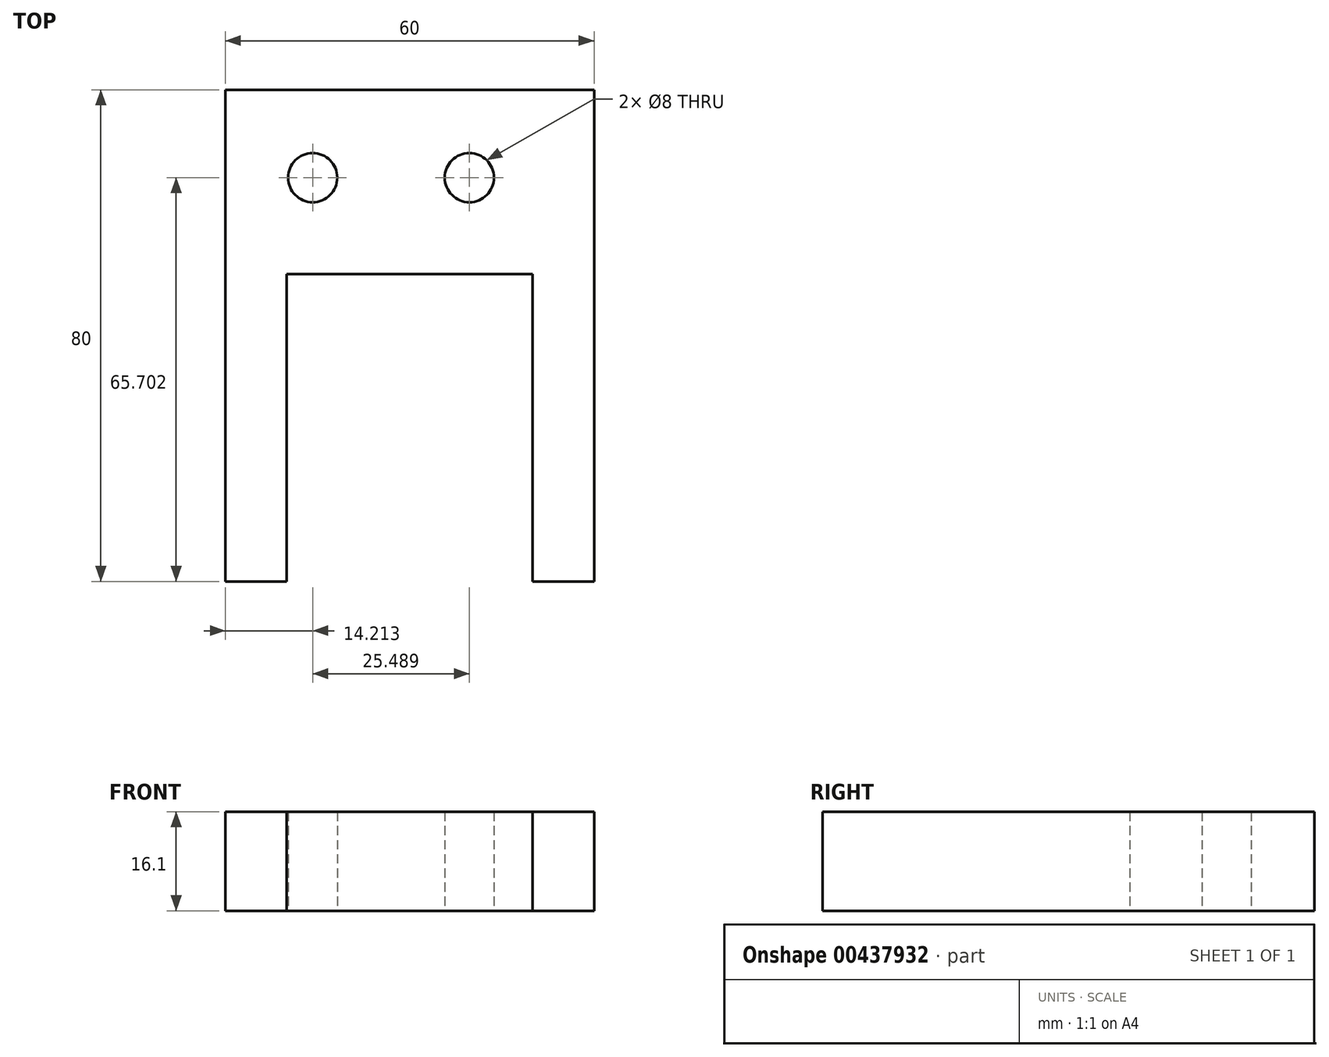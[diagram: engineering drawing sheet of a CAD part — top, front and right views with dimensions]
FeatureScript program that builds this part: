
annotation { "Feature Type Name" : "Feature", "Feature Type Description" : "" }
export const myFeature = defineFeature(function(context is Context, id is Id, definition is map)
    precondition{}
    {
        {
            var Q0;
            Q0=qCreatedBy(makeId("Top.planeOp"),FACE);
            var sketch = newSketch(context, id + "F0", { "sketchPlane" : qUnion([Q0])});
            skLineSegment(sketch, "E0.bottom", {"start": v(-53.14, 69.79) * mm, "end": v(6.86, 69.79) * mm});
            skLineSegment(sketch, "E0.top", {"start": v(-53.14, 39.79) * mm, "end": v(6.86, 39.79) * mm});
            skLineSegment(sketch, "E0.left", {"start": v(-53.14, 69.79) * mm, "end": v(-53.14, 39.79) * mm});
            skLineSegment(sketch, "E0.right", {"start": v(6.86, 69.79) * mm, "end": v(6.86, 39.79) * mm});
            skLineSegment(sketch, "E1.bottom", {"start": v(-53.14, 39.79) * mm, "end": v(-43.14, 39.79) * mm});
            skLineSegment(sketch, "E1.top", {"start": v(-53.14, -10.21) * mm, "end": v(-43.14, -10.21) * mm});
            skLineSegment(sketch, "E1.left", {"start": v(-53.14, 39.79) * mm, "end": v(-53.14, -10.21) * mm});
            skLineSegment(sketch, "E1.right", {"start": v(-43.14, 39.79) * mm, "end": v(-43.14, -10.21) * mm});
            skLineSegment(sketch, "E2.bottom", {"start": v(6.86, 39.79) * mm, "end": v(-3.14, 39.79) * mm});
            skLineSegment(sketch, "E2.top", {"start": v(6.86, -10.21) * mm, "end": v(-3.14, -10.21) * mm});
            skLineSegment(sketch, "E2.left", {"start": v(6.86, 39.79) * mm, "end": v(6.86, -10.21) * mm});
            skLineSegment(sketch, "E2.right", {"start": v(-3.14, 39.79) * mm, "end": v(-3.14, -10.21) * mm});
            skCircle(sketch, "E3", {"center": v(-38.93, 55.5) * mm, "radius": 4 * mm});
            skCircle(sketch, "E4", {"center": v(-13.44, 55.5) * mm, "radius": 4 * mm});
            skSolve(sketch);
        }
        {
            var Q0;
            Q0 = qSketchRegion(id + "F0", true);
            extrude(context, id + "F1", {"entities" : qUnion([Q0]), "depth" : 8.05 * mm});
        }
        {
            var Q0;
            Q0=makeQuery(id+"F1.opExtrude","CAP_FACE",FACE,{"disambiguationData":[OSD([sQuery(id+"F0.wireOp",EDGE,"E0.bottom"),sQuery(id+"F0.wireOp",EDGE,"E0.top"),sQuery(id+"F0.wireOp",EDGE,"E0.left"),sQuery(id+"F0.wireOp",EDGE,"E0.right"),sQuery(id+"F0.wireOp",EDGE,"E1.top"),sQuery(id+"F0.wireOp",EDGE,"E1.left"),sQuery(id+"F0.wireOp",EDGE,"E1.right"),sQuery(id+"F0.wireOp",EDGE,"E2.top"),sQuery(id+"F0.wireOp",EDGE,"E2.left"),sQuery(id+"F0.wireOp",EDGE,"E2.right"),sQuery(id+"F0.wireOp",EDGE,"E3"),sQuery(id+"F0.wireOp",EDGE,"E4")])],"isStart":false});
            extrude(context, id + "F2", {"entities" : qUnion([Q0]), "operationType" : NewBodyOperationType.ADD, "depth" : 8.05 * mm});
        }
    });
